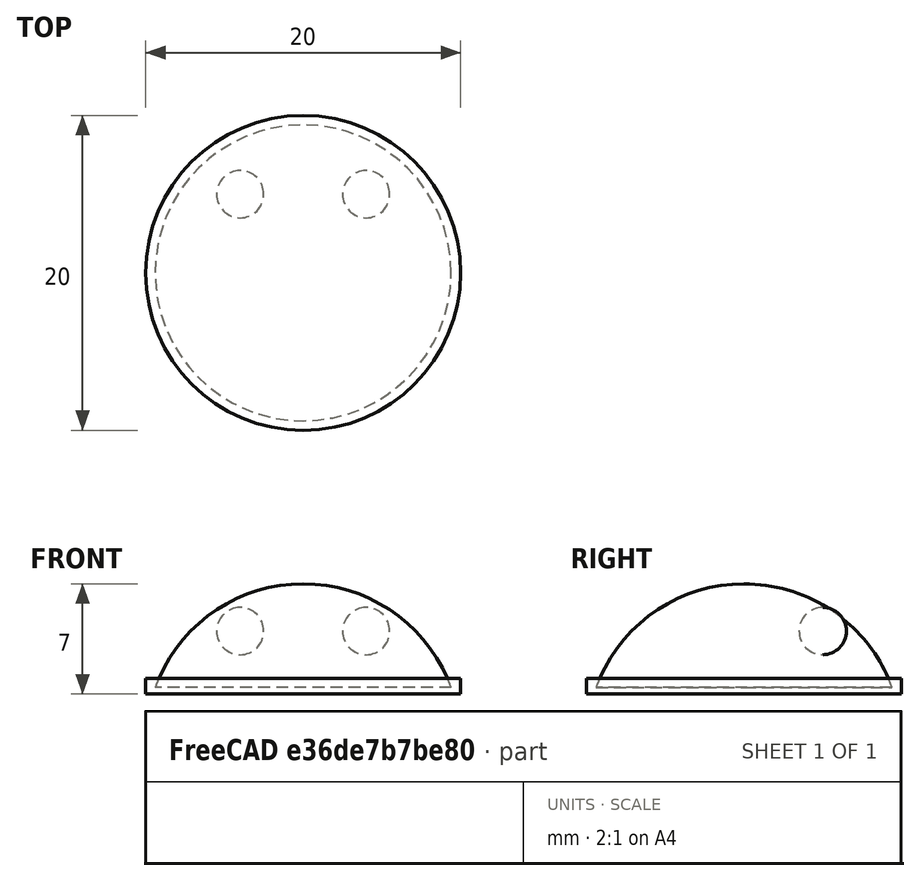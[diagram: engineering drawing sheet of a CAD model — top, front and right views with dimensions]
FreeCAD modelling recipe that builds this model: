
FCSTD DOCUMENT  (FreeCAD 0.21R33694 (Git))
Label: OJT1_T013_robot
License: All rights reserved
LicenseURL: https://en.wikipedia.org/wiki/All_rights_reserved
objects: Part::Sphere×3, Part::Cylinder×1
note: 4 computed .brp shape members not serialized (recipe doc carries the construction recipe); baked Part::Feature solids carry a one-line shape summary decoded from their .brp

FEATURE [Part::Sphere] Sphere  label="Esfera"
  Angle1 = 20
  Angle2 = 90
  Angle3 = 360
  AttacherType = Attacher::AttachEngine3D
  Placement = pos=(0,0,-3) rot=(0,0,1;0rad)
  Radius = 10
FEATURE [Part::Cylinder] Cylinder  label="Cilindre"
  Angle = 360
  AttacherType = Attacher::AttachEngine3D
  FirstAngle = 0
  Height = 1
  Radius = 10
  SecondAngle = 0
FEATURE [Part::Sphere] Sphere001  label="Esfera001"
  Angle1 = -90
  Angle2 = 90
  Angle3 = 360
  AttacherType = Attacher::AttachEngine3D
  Placement = pos=(4,5,4) rot=(0,0,1;0rad)
  Radius = 1.5
FEATURE [Part::Sphere] Sphere002  label="Esfera002"
  Angle1 = -90
  Angle2 = 90
  Angle3 = 360
  AttacherType = Attacher::AttachEngine3D
  Placement = pos=(-4,5,4) rot=(0,0,1;0rad)
  Radius = 1.5
